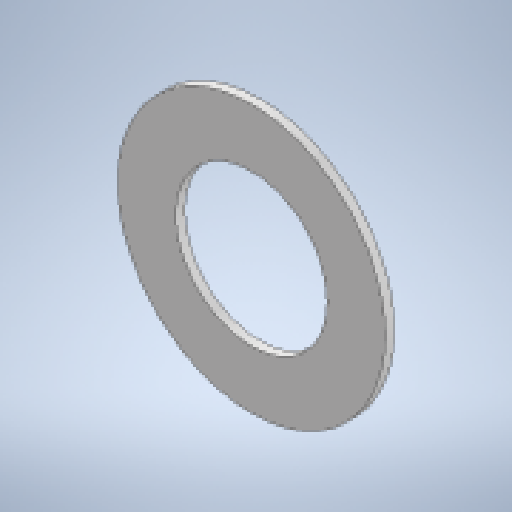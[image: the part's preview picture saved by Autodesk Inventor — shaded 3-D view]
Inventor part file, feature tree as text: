
AUTODESK INVENTOR PART (.ipt)
format: ipt  version: 2023 (Build 270158000, 158)  size: 130,560 bytes
history: native  units: mm
features: extrude x1, sketch x1
ambient origin geometry x8: Origin, YZ Plane, XZ Plane, XY Plane, X Axis, Y Axis, Z Axis, Center Point
bodies: Solid1 (feature_tree)
feature tree (2):
  extrude  "Extrusion1"  Depth=0.2mm
  sketch  "Sketch1"  dims[d0=3.4mm d1=6.0mm d2=0.2mm d3=0.0mm]
